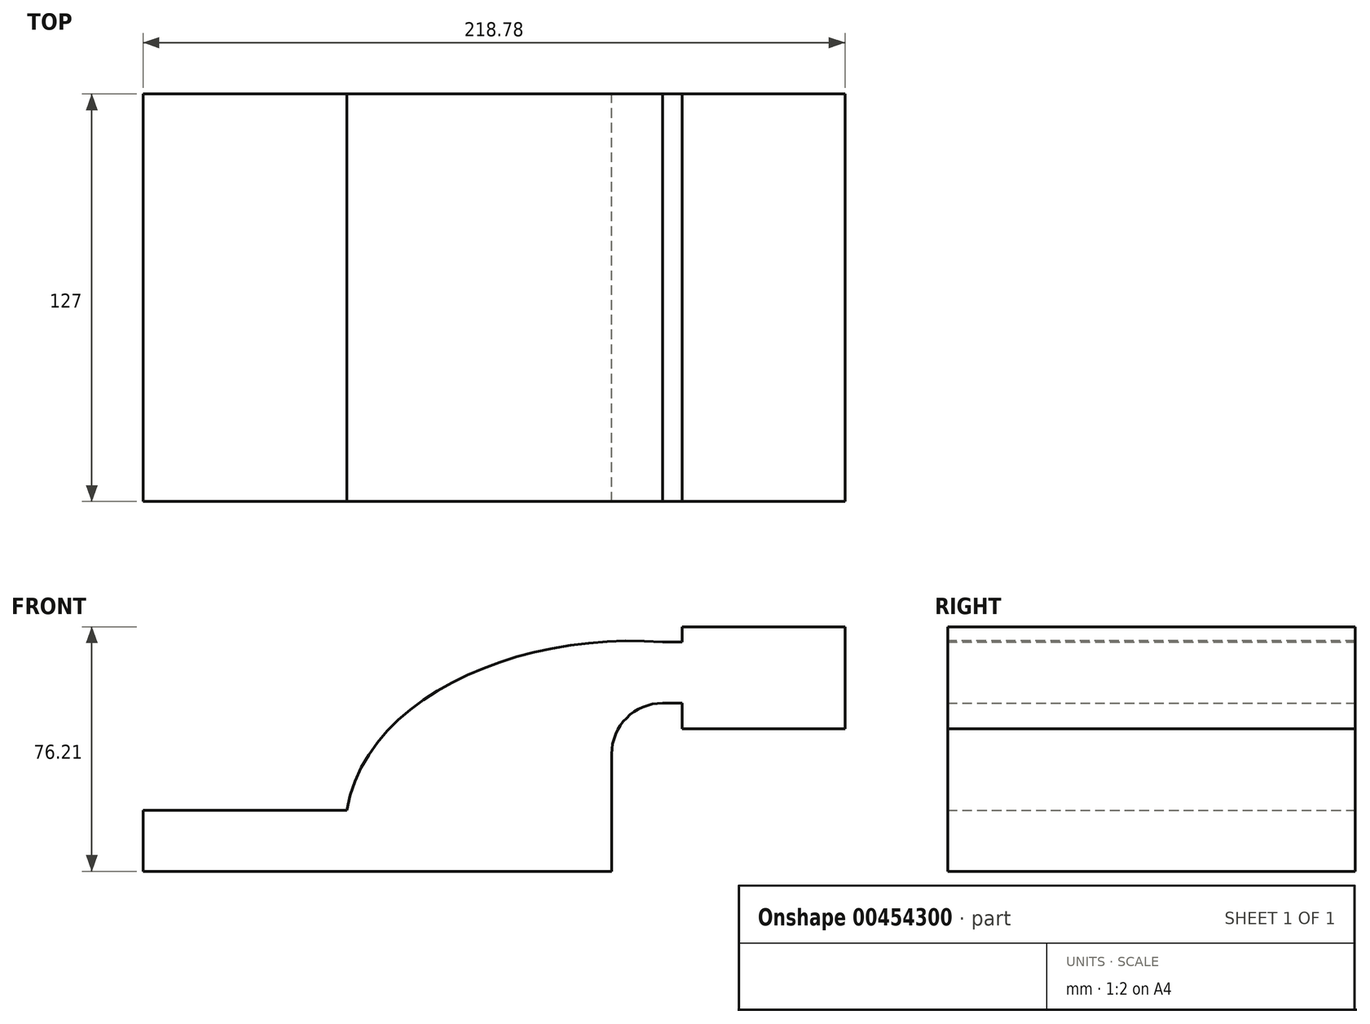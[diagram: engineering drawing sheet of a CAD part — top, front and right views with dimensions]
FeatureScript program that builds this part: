
annotation { "Feature Type Name" : "Feature", "Feature Type Description" : "" }
export const myFeature = defineFeature(function(context is Context, id is Id, definition is map)
    precondition{}
    {
        {
            var Q0;
            Q0=qCreatedBy(makeId("Front.planeOp"),FACE);
            var sketch = newSketch(context, id + "F0", { "sketchPlane" : qUnion([Q0])});
            skLineSegment(sketch, "E0.bottom", {"start": v(-41.28, -9.53) * mm, "end": v(41.28, -9.53) * mm});
            skLineSegment(sketch, "E0.top", {"start": v(-41.28, 9.52) * mm, "end": v(41.28, 9.52) * mm});
            skLineSegment(sketch, "E0.left", {"start": v(-41.27, -9.53) * mm, "end": v(-41.28, 9.52) * mm});
            skLineSegment(sketch, "E0.right", {"start": v(41.28, -9.53) * mm, "end": v(41.28, 9.52) * mm});
            skPoint(sketch, "E0.middle", {"position": v(0, 0) * mm});
            skLineSegment(sketch, "E1.bottom", {"start": v(63.2, 66.67) * mm, "end": v(114, 66.67) * mm});
            skLineSegment(sketch, "E1.top", {"start": v(63.2, 34.93) * mm, "end": v(114, 34.93) * mm});
            skLineSegment(sketch, "E1.left", {"start": v(114, 34.92) * mm, "end": v(114, 66.67) * mm});
            skLineSegment(sketch, "E1.right", {"start": v(63.2, 34.92) * mm, "end": v(63.2, 66.67) * mm});
            skPoint(sketch, "E1.middle", {"position": v(88.6, 50.8) * mm});
            skLineSegment(sketch, "E2", {"start": v(41.27, 9.52) * mm, "end": v(41.27, 27) * mm});
            skArc(sketch, "E3", {"start": v(41.27, 27) * mm, "mid": v(45.92, 38.23) * mm, "end": v(57.15, 42.88) * mm});
            skLineSegment(sketch, "E4", {"start": v(57.15, 42.88) * mm, "end": v(87.96, 42.88) * mm});
            skLineSegment(sketch, "E5.0", {"start": v(57.15, 61.93) * mm, "end": v(87.96, 61.93) * mm});
            skArc(sketch, "E5.1", {"start": v(22.22, 27) * mm, "mid": v(32.45, 51.7) * mm, "end": v(57.15, 61.93) * mm});
            skLineSegment(sketch, "E5.2", {"start": v(22.22, 9.52) * mm, "end": v(22.22, 27) * mm});
            skLineSegment(sketch, "E6", {"start": v(88.6, 50.8) * mm, "end": v(88.6, 66.67) * mm});
            skLineSegment(sketch, "E7", {"start": v(87.96, 42.88) * mm, "end": v(88.6, 66.67) * mm});
            skLineSegment(sketch, "E8", {"start": v(-221.5, 93.61) * mm, "end": v(-218.44, 88.82) * mm});
            skFitSpline(sketch, "E9", {"points": [v(-41.28, 9.53) * mm, v(57.15, 61.93) * mm], "startDerivative": vector(18.48, 107.8) * mm, "endDerivative": vector(131.27, -9.99) * mm});
            skSolve(sketch);
        }
        {
            var Q0;
            Q0=makeQuery(id+"F0.imprint","IMPRINT",FACE,{"disambiguationData":[TD([[makeQuery(id+"F0.imprint","IMPRINT",EDGE,{"derivedFrom":sQuery(id+"F0.wireOp",EDGE,"E0.bottom")}),1.0]])]});
            extrude(context, id + "F1", {"entities" : qUnion([Q0]), "endBound" : BoundingType.SYMMETRIC, "depth" : 127 * mm});
        }
        {
            var Q0;
            Q0 = qSketchRegion(id + "F0", true);
            extrude(context, id + "F2", {"entities" : qUnion([Q0]), "operationType" : NewBodyOperationType.ADD, "endBound" : BoundingType.SYMMETRIC, "depth" : 127 * mm});
        }
        {
            var Q0;
            Q0=makeQuery(id+"F1.opExtrude","SWEPT_FACE",FACE,{"disambiguationData":[OSD([sQuery(id+"F0.wireOp",EDGE,"E0.left")])]});
            extrude(context, id + "F3", {"entities" : qUnion([Q0]), "operationType" : NewBodyOperationType.ADD, "endBound" : BoundingType.SYMMETRIC, "depth" : 127 * mm});
        }
    });
